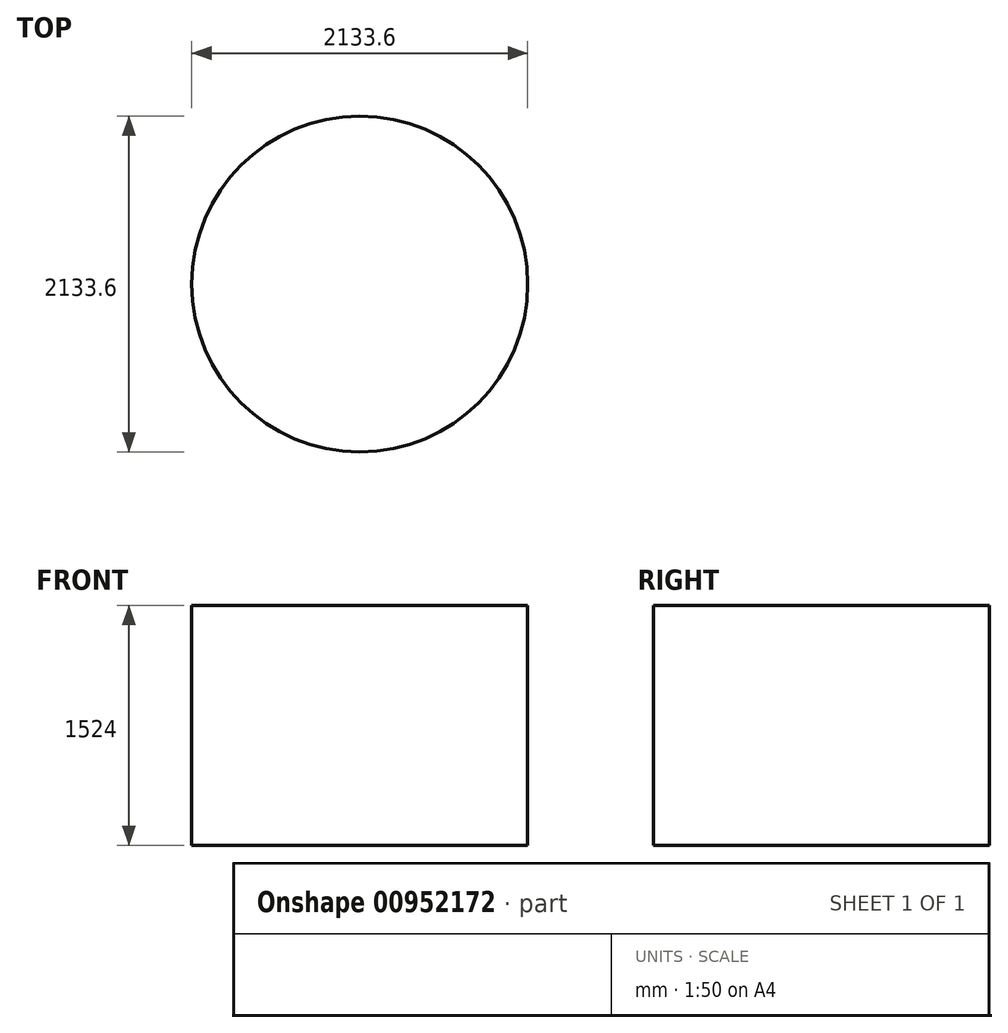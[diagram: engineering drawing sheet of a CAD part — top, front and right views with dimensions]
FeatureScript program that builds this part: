
annotation { "Feature Type Name" : "Feature", "Feature Type Description" : "" }
export const myFeature = defineFeature(function(context is Context, id is Id, definition is map)
    precondition{}
    {
        {
            var Q0;
            Q0=qCreatedBy(makeId("Top.planeOp"),FACE);
            var sketch = newSketch(context, id + "F0", { "sketchPlane" : qUnion([Q0])});
            skCircle(sketch, "E0", {"center": v(0, 0) * mm, "radius": 1066.8 * mm});
            skSolve(sketch);
        }
        {
            var Q0;
            Q0=makeQuery(id+"F0.imprint","IMPRINT",FACE,{"disambiguationData":[TD([[makeQuery(id+"F0.imprint","IMPRINT",EDGE,{"derivedFrom":sQuery(id+"F0.wireOp",EDGE,"E0")}),1.0]])]});
            extrude(context, id + "F1", {"entities" : qUnion([Q0]), "depth" : 1524 * mm, "offsetDistance" : 25.4 * mm});
        }
    });
